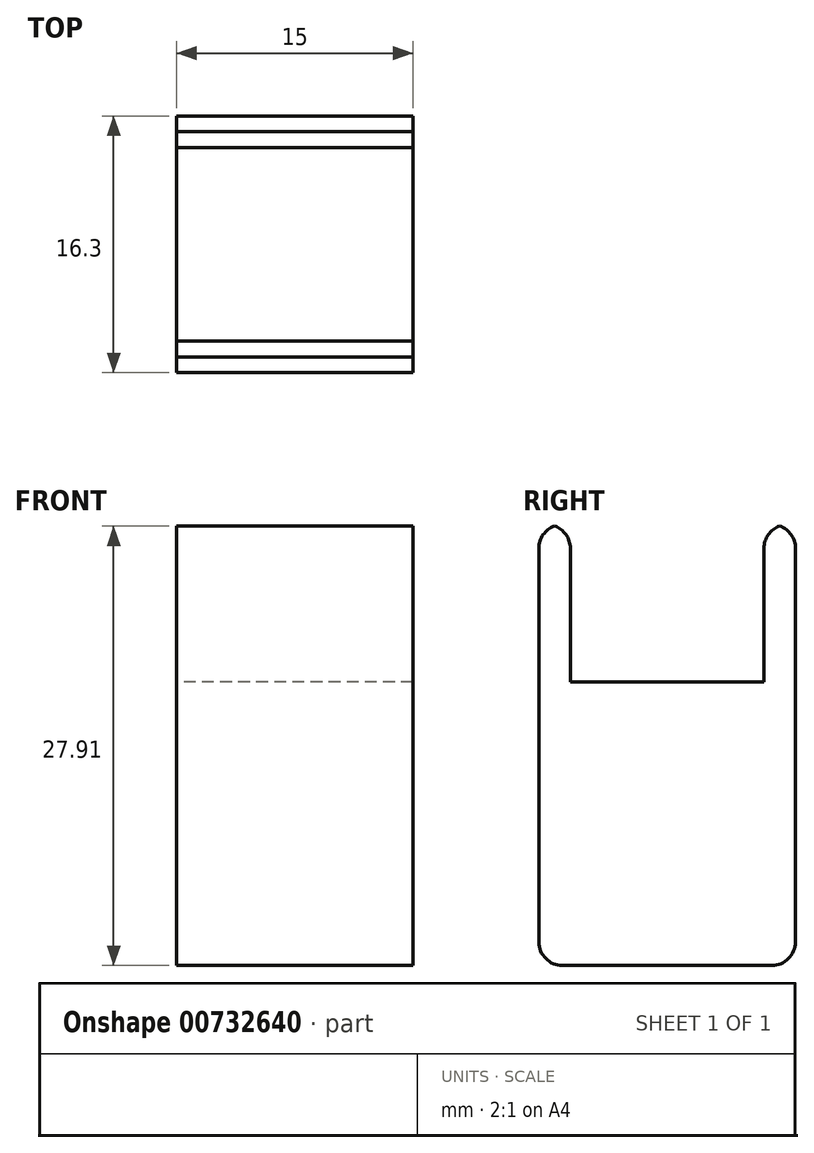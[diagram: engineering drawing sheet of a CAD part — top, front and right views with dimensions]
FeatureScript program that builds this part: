
annotation { "Feature Type Name" : "Feature", "Feature Type Description" : "" }
export const myFeature = defineFeature(function(context is Context, id is Id, definition is map)
    precondition{}
    {
        {
            var Q0;
            Q0=qCreatedBy(makeId("Right.planeOp"),FACE);
            var sketch = newSketch(context, id + "F0", { "sketchPlane" : qUnion([Q0])});
            skPoint(sketch, "E0.middle", {"position": v(0, 0) * mm});
            skLineSegment(sketch, "E1", {"start": v(0, 0) * mm, "end": v(6.15, 0) * mm});
            skLineSegment(sketch, "E2", {"start": v(6.15, 0) * mm, "end": v(6.15, 10) * mm});
            skLineSegment(sketch, "E3", {"start": v(0, -18) * mm, "end": v(8.15, -18) * mm});
            skLineSegment(sketch, "E4", {"start": v(8.15, -18) * mm, "end": v(8.15, 10) * mm});
            skLineSegment(sketch, "E5", {"start": v(8.15, 10) * mm, "end": v(6.15, 10) * mm});
            skLineSegment(sketch, "E6.MirrorCS", {"start": v(-8.15, 10) * mm, "end": v(-6.15, 10) * mm});
            skLineSegment(sketch, "E7.MirrorCS", {"start": v(-8.15, -18) * mm, "end": v(-8.15, 10) * mm});
            skLineSegment(sketch, "E8.MirrorCS", {"start": v(-6.15, 0) * mm, "end": v(-6.15, 10) * mm});
            skLineSegment(sketch, "E9.MirrorCS", {"start": v(0, 0) * mm, "end": v(-6.15, 0) * mm});
            skLineSegment(sketch, "E10.MirrorCS", {"start": v(0, -18) * mm, "end": v(-8.15, -18) * mm});
            skSolve(sketch);
        }
        {
            var Q0;
            Q0 = qSketchRegion(id + "F0", true);
            extrude(context, id + "F1", {"entities" : qUnion([Q0]), "endBound" : BoundingType.SYMMETRIC, "depth" : 15 * mm, "offsetDistance" : 25 * mm});
        }
        {
            var Q0;
            Q0=makeQuery(id+"F1.opExtrude","SWEPT_EDGE",EDGE,{"disambiguationData":[OSD([sQuery(id+"F0.wireOp",EDGE,"E6.MirrorCS"),sQuery(id+"F0.wireOp",EDGE,"E7.MirrorCS")])]});
            var Q1;
            Q1=makeQuery(id+"F1.opExtrude","SWEPT_EDGE",EDGE,{"disambiguationData":[OSD([sQuery(id+"F0.wireOp",EDGE,"E6.MirrorCS"),sQuery(id+"F0.wireOp",EDGE,"E8.MirrorCS")])]});
            var Q2;
            Q2=makeQuery(id+"F1.opExtrude","SWEPT_EDGE",EDGE,{"disambiguationData":[OSD([sQuery(id+"F0.wireOp",EDGE,"E2"),sQuery(id+"F0.wireOp",EDGE,"E5")])]});
            var Q3;
            Q3=makeQuery(id+"F1.opExtrude","SWEPT_EDGE",EDGE,{"disambiguationData":[OSD([sQuery(id+"F0.wireOp",EDGE,"E4"),sQuery(id+"F0.wireOp",EDGE,"E5")])]});
            var Q4;
            Q4=makeQuery(id+"F1.opExtrude","SWEPT_EDGE",EDGE,{"disambiguationData":[OSD([sQuery(id+"F0.wireOp",EDGE,"E7.MirrorCS"),sQuery(id+"F0.wireOp",EDGE,"E10.MirrorCS")])]});
            var Q5;
            Q5=makeQuery(id+"F1.opExtrude","SWEPT_EDGE",EDGE,{"disambiguationData":[OSD([sQuery(id+"F0.wireOp",EDGE,"E3"),sQuery(id+"F0.wireOp",EDGE,"E4")])]});
            fillet(context, id + "F2", {"entities" : qUnion([Q0, Q1, Q2, Q3, Q4, Q5]), "radius" : 1.5 * mm, "tangentPropagation" : true, "defaultsChanged" : true, "vertexSettings" : [], "allowEdgeOverflow" : false});
        }
    });
